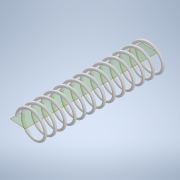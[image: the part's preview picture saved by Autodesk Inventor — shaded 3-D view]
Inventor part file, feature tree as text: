
AUTODESK INVENTOR PART (.ipt)
format: ipt  version: 2021 (Build 250183000, 183)  size: 688,128 bytes
history: native  units: mm
features: other x3, sketch x3, sweep x1, extrude x1
ambient origin geometry x8: Origin, YZ Plane, XZ Plane, XY Plane, X Axis, Y Axis, Z Axis, Center Point
bodies: Body1 (feature_tree)
feature tree (8):
  other  "Bryła1"
  sketch  "Szkic 3D1"
  other  "Płaszczyzna konstrukcyjna1"
  sweep  "Przeciągnięcie1"
  extrude  "Wyciągnięcie proste1"  TaperAngle=0.0deg  [1 undecoded]
  other  "Krzywa śrubowa1"
  sketch  "Szkic1"
  sketch  "Szkic2"
note: 1 required parameter value undecoded (feature->parameter linkage not recoverable at this tier; creation-order binding heuristic only, values carry confidence <= 0.55)
